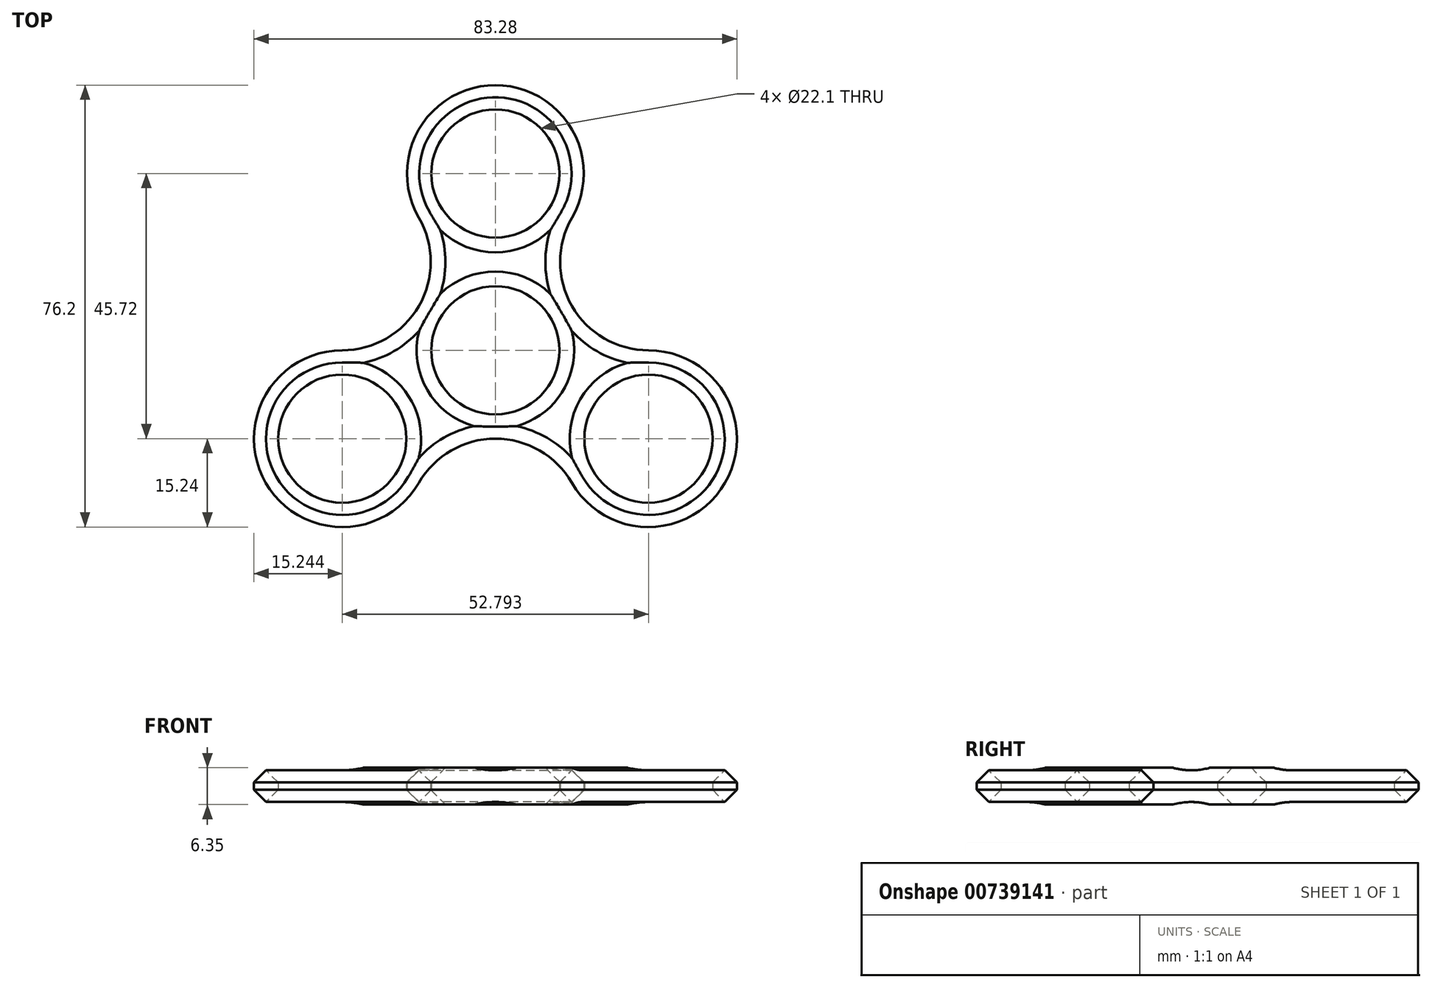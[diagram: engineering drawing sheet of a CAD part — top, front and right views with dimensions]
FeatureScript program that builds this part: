
annotation { "Feature Type Name" : "Feature", "Feature Type Description" : "" }
export const myFeature = defineFeature(function(context is Context, id is Id, definition is map)
    precondition{}
    {
        {
            var Q0;
            Q0=qCreatedBy(makeId("Top.planeOp"),FACE);
            var sketch = newSketch(context, id + "F0", { "sketchPlane" : qUnion([Q0])});
            skCircle(sketch, "E0", {"center": v(0, 0) * mm, "radius": 11.05 * mm});
            skLineSegment(sketch, "E1", {"start": v(0, 0) * mm, "end": v(0, 11.05) * mm});
            skCircle(sketch, "E2", {"center": v(0, 30.48) * mm, "radius": 11.05 * mm});
            skArc(sketch, "E3", {"start": v(13.2, 22.86) * mm, "mid": v(0, 45.72) * mm, "end": v(-13.2, 22.86) * mm});
            skCircle(sketch, "E4.1.0", {"center": v(-26.4, -15.24) * mm, "radius": 11.05 * mm});
            skArc(sketch, "E4.1.1", {"start": v(-26.4, 0) * mm, "mid": v(-39.6, -22.86) * mm, "end": v(-13.2, -22.86) * mm});
            skCircle(sketch, "E4.2.0", {"center": v(26.4, -15.24) * mm, "radius": 11.05 * mm});
            skArc(sketch, "E4.2.1", {"start": v(13.2, -22.86) * mm, "mid": v(39.6, -22.86) * mm, "end": v(26.4, 0) * mm});
            skArc(sketch, "E5", {"start": v(-26.4, 0) * mm, "mid": v(-13.2, 7.62) * mm, "end": v(-13.2, 22.86) * mm});
            skArc(sketch, "E6.1.0", {"start": v(13.2, -22.86) * mm, "mid": v(0, -15.24) * mm, "end": v(-13.2, -22.86) * mm});
            skArc(sketch, "E6.2.0", {"start": v(13.2, 22.86) * mm, "mid": v(13.2, 7.62) * mm, "end": v(26.4, 0) * mm});
            skSolve(sketch);
        }
        {
            var Q0;
            Q0=makeQuery(id+"F0.imprint","IMPRINT",FACE,{"disambiguationData":[TD([[makeQuery(id+"F0.imprint","IMPRINT",EDGE,{"derivedFrom":sQuery(id+"F0.wireOp",EDGE,"E0")}),-1.0]])]});
            extrude(context, id + "F1", {"entities" : qUnion([Q0]), "depth" : 6.35 * mm, "offsetDistance" : 25.4 * mm});
        }
        {
            var Q0;
            Q0=makeQuery(id+"F1.opExtrude","CAP_FACE",FACE,{"disambiguationData":[OSD([sQuery(id+"F0.wireOp",EDGE,"E0"),sQuery(id+"F0.wireOp",EDGE,"E2"),sQuery(id+"F0.wireOp",EDGE,"E3"),sQuery(id+"F0.wireOp",EDGE,"E4.1.0"),sQuery(id+"F0.wireOp",EDGE,"E4.1.1"),sQuery(id+"F0.wireOp",EDGE,"E4.2.0"),sQuery(id+"F0.wireOp",EDGE,"E4.2.1"),sQuery(id+"F0.wireOp",EDGE,"E5"),sQuery(id+"F0.wireOp",EDGE,"E6.1.0"),sQuery(id+"F0.wireOp",EDGE,"E6.2.0")])],"isStart":false});
            var Q1;
            Q1=makeQuery(id+"F1.opExtrude","CAP_FACE",FACE,{"disambiguationData":[OSD([sQuery(id+"F0.wireOp",EDGE,"E0"),sQuery(id+"F0.wireOp",EDGE,"E2"),sQuery(id+"F0.wireOp",EDGE,"E3"),sQuery(id+"F0.wireOp",EDGE,"E4.1.0"),sQuery(id+"F0.wireOp",EDGE,"E4.1.1"),sQuery(id+"F0.wireOp",EDGE,"E4.2.0"),sQuery(id+"F0.wireOp",EDGE,"E4.2.1"),sQuery(id+"F0.wireOp",EDGE,"E5"),sQuery(id+"F0.wireOp",EDGE,"E6.1.0"),sQuery(id+"F0.wireOp",EDGE,"E6.2.0")])],"isStart":true});
            chamfer(context, id + "F2", {"entities" : qUnion([Q0, Q1]), "width" : 2.54 * mm, "tangentPropagation" : true});
        }
    });
